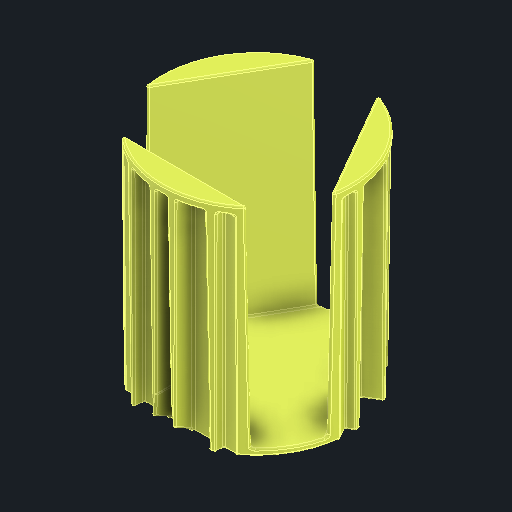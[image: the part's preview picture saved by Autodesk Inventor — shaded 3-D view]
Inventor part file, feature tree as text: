
AUTODESK INVENTOR PART (.ipt)
format: ipt  version: 2025 (Build 290162000, 162)  size: 865,792 bytes
history: native  units: in
note: dims shown in document units (in); Inventor stores cm internally (conversion verified against a paired STEP export)
features: fillet x1
ambient origin geometry x8: Origin, YZ Plane, XZ Plane, XY Plane, X Axis, Y Axis, Z Axis, Center Point
bodies: Solid1 (feature_tree)
feature tree (1):
  fillet  "Fillet21"  [1 undecoded]
note: 1 required parameter value undecoded (feature->parameter linkage not recoverable at this tier; creation-order binding heuristic only, values carry confidence <= 0.55)
